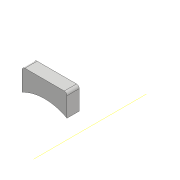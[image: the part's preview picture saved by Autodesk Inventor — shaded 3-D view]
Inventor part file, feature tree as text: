
AUTODESK INVENTOR PART (.ipt)
format: ipt  version: 2018 (Build 220112000, 112)  size: 1,485,824 bytes
history: native  units: mm
features: sketch x39, projected_geometry x37, extrude x34, fillet x13, hole x4, chamfer x4, mirror x1, other x1, revolve x1, shell x1, pattern_circular x1
ambient origin geometry x8: Origin, YZ Plane, XZ Plane, XY Plane, X Axis, Y Axis, Z Axis, Center Point
bodies: Solid1 (feature_tree), Solid2 (feature_tree)
feature tree (136):
  extrude  "Extrusion1"  Depth=45.0mm
  extrude  "Extrusion2"  Depth=2.25mm
  hole  "Hole1"  [1 undecoded]
  hole  "Hole2"  [1 undecoded]
  fillet  "Fillet1"  Radius=14.0mm
  extrude  "Extrusion3"  Depth=18.5mm
  extrude  "Extrusion4"  Depth=10.0mm
  extrude  "Extrusion5"  Depth=2.195mm
  extrude  "Extrusion6"  Depth=20.5mm
  hole  "Hole3"  [1 undecoded]
  extrude  "Extrusion7"  Depth=0.5mm
  extrude  "Extrusion8"  Depth=5.0mm TaperAngle=0.0deg
  extrude  "Extrusion9"  Depth=10.0mm
  extrude  "Extrusion10"  Depth=10.0mm
  extrude  "Extrusion11"  Depth=14.5mm
  extrude  "Extrusion12"  Depth=14.5mm
  extrude  "Extrusion13"  Depth=5.0mm
  extrude  "Extrusion14"  Depth=2.25mm
  extrude  "Extrusion15"  Depth=5.0mm
  extrude  "Extrusion16"  Depth=9.0mm
  extrude  "Extrusion17"  Depth=4.0mm
  chamfer  "Chamfer1"  Distance=1.0mm
  fillet  "Fillet7"  Radius=20.7mm
  fillet  "Fillet8"  Radius=32.0mm
  mirror  "Mirror1"
  extrude  "Extrusion18"  Depth=1.0mm TaperAngle=0.0deg
  extrude  "Extrusion19"  Depth=8.0mm
  extrude  "Extrusion20"  Depth=0.2mm TaperAngle=0.0deg
  extrude  "Extrusion21"  Depth=0.5mm TaperAngle=0.0deg
  extrude  "Extrusion22"  Depth=3.0mm TaperAngle=0.0deg
  extrude  "Extrusion23"  Depth=0.2mm TaperAngle=0.0deg
  extrude  "Extrusion24"  Depth=2.5mm TaperAngle=45.0deg
  sketch  "Sketch35"  dims[d91=8.0mm d92=0.0mm d93=3.0mm d94=0.0mm]
  other  "Work Axis1"
  revolve  "Revolution1"  [1 undecoded]
  extrude  "Extrusion25"  Depth=4.0mm TaperAngle=0.0deg
  extrude  "Extrusion26"  Depth=19.2mm TaperAngle=0.0deg
  shell  "Shell1"  Thickness=52.1mm
  extrude  "Extrusion27"  Depth=6.8mm
  extrude  "Extrusion28"  Depth=25.0mm
  chamfer  "Chamfer4"  Distance=6.9mm
  chamfer  "Chamfer5"  Distance=2.5mm
  extrude  "Extrusion29"  Depth=10.0mm
  pattern_circular  "Circular Pattern1"  Angle=90.0deg  [1 undecoded]
  fillet  "Fillet11"  Radius=5.0mm
  fillet  "Fillet12"  Radius=105.0mm
  fillet  "Fillet13"  Radius=105.0mm
  fillet  "Fillet14"  Radius=5.0mm
  chamfer  "Chamfer6"  Distance=12.8mm
  hole  "Hole6"  [1 undecoded]
  extrude  "Extrusion30"  Depth=10.0mm
  fillet  "Fillet15"  Radius=12.8mm
  extrude  "Extrusion31"  Depth=10.0mm
  fillet  "Fillet16"  Radius=20.0mm
  extrude  "Extrusion32"  Depth=10.0mm
  fillet  "Fillet17"  Radius=6.0mm
  fillet  "Fillet18"  Radius=40.0mm
  fillet  "Fillet19"  Radius=8.0mm
  fillet  "Fillet20"  Radius=40.0mm
  extrude  "Extrusion33"  Depth=10.0mm TaperAngle=0.0deg
  extrude  "Extrusion34"  Depth=10.0mm TaperAngle=45.0deg
  sketch  "Sketch1"  dims[d0=24.5mm d1=45.0mm]
  sketch  "Sketch2"  dims[d2=1.95mm d3=0.0mm d4=2.25mm]
  projected_geometry  "Projected Loop1"
  sketch  "Sketch3"  dims[d5=20.0mm d6=2.25mm]
  projected_geometry  "Projected Loop2"
  sketch  "Sketch4"  dims[d7=5.25mm d8=5.25mm d9=14.0mm]
  projected_geometry  "Projected Loop3"
  sketch  "Sketch5"  dims[d10=5.25mm d11=18.5mm]
  projected_geometry  "Projected Loop4"
  sketch  "Sketch6"  dims[d12=10.0mm d13=0.0mm d14=20.5mm]
  projected_geometry  "Projected Loop5"
  sketch  "Sketch7"  dims[d15=2.0mm d16=2.195mm]
  projected_geometry  "Projected Loop6"
  sketch  "Sketch8"  dims[d17=2.0mm]
  projected_geometry  "Projected Loop7"
  sketch  "Sketch9"  dims[d18=2.4mm d19=6.0mm d20=4.4mm d21=2.0mm d22=90.0deg d23=8.0mm d24=20.594885mm d25=20.5mm]
  projected_geometry  "Projected Loop8"
  projected_geometry  "Projected Loop9"
  sketch  "Sketch10"  dims[d26=26.65mm d27=2.0mm]
  projected_geometry  "Projected Loop10"
  projected_geometry  "Projected Loop11"
  sketch  "Sketch11"  dims[d28=2.0mm]
  projected_geometry  "Projected Loop12"
  sketch  "Sketch12"  dims[d29=2.4mm d30=6.0mm d31=4.4mm d32=2.0mm d33=90.0deg d34=8.0mm d35=20.594885mm d36=0.5mm]
  sketch  "Sketch13"  dims[d37=18.0mm d38=5.0mm d39=0.0mm]
  sketch  "Sketch14"  dims[d41=10.0mm d42=0.0mm d43=24.5mm]
  projected_geometry  "Projected Loop13"
  sketch  "Sketch15"  dims[d44=1.15mm d45=0.0mm d46=10.0mm]
  sketch  "Sketch16"  dims[d47=21.0mm d48=14.5mm]
  projected_geometry  "Projected Loop14"
  sketch  "Sketch17"  dims[d49=20.0mm d50=14.5mm]
  projected_geometry  "Projected Loop15"
  sketch  "Sketch18"  dims[d51=24.5mm d52=5.0mm]
  projected_geometry  "Projected Loop16"
  sketch  "Sketch19"  dims[d53=5.0mm d54=2.25mm]
  projected_geometry  "Projected Loop17"
  sketch  "Sketch20"  dims[d55=2.25mm d56=5.0mm]
  projected_geometry  "Projected Loop18"
  sketch  "Sketch22"  dims[d57=5.0mm d58=9.0mm]
  sketch  "Sketch25"  dims[d59=14.75mm d60=4.0mm d61=1.0mm d62=0.0mm d63=20.7mm]
  sketch  "Sketch27"  dims[d64=2.4mm d65=6.0mm d66=4.4mm d67=2.0mm d68=90.0deg d69=8.0mm d70=20.594885mm d72=32.0mm]
  projected_geometry  "Projected Loop22"
  sketch  "Sketch28"  dims[d73=5.0mm d74=0.0mm d75=1.0mm d76=0.0mm]
  projected_geometry  "Projected Loop23"
  sketch  "Sketch29"  dims[d77=12.25mm d78=0.0mm d80=8.0mm]
  projected_geometry  "Projected Loop24"
  sketch  "Sketch30"  dims[d81=4.5mm d82=0.0mm d84=0.2mm d85=0.0mm]
  projected_geometry  "Projected Loop25"
  sketch  "Sketch33"  dims[d86=21.0mm d87=0.5mm d88=0.0mm]
  projected_geometry  "Projected Loop26"
  sketch  "Sketch36"  dims[d95=5.0mm d96=0.0mm d98=0.2mm d99=0.0mm]
  projected_geometry  "Projected Loop27"
  sketch  "Sketch37"  dims[d100=0.2mm d101=0.0mm d102=2.5mm d103=2.0mm d104=45.0deg]
  projected_geometry  "Projected Loop28"
  sketch  "Sketch38"  dims[d105=1.5mm d114=0.5mm]
  projected_geometry  "Projected Loop29"
  projected_geometry  "Projected Loop30"
  projected_geometry  "Projected Loop31"
  projected_geometry  "Projected Loop32"
  sketch  "Sketch39"  dims[d115=22.55mm d116=0.0mm d128=4.0mm d129=0.0mm]
  projected_geometry  "Projected Loop33"
  projected_geometry  "Projected Loop34"
  sketch  "Sketch40"  dims[d130=4.0mm d131=0.0mm d132=19.2mm d133=0.0mm d134=52.1mm]
  projected_geometry  "Projected Loop35"
  sketch  "Sketch41"  dims[d135=6.8mm d136=0.0mm d137=9.0mm]
  projected_geometry  "Projected Loop36"
  sketch  "Sketch42"  dims[d138=9.0mm d139=25.0mm d140=6.9mm d141=0.0mm]
  sketch  "Sketch43"  dims[d142=5.2mm]
  projected_geometry  "Projected Loop37"
  sketch  "Sketch44"  dims[d143=5.2mm]
  projected_geometry  "Projected Loop38"
  sketch  "Sketch45"  dims[d144=5.2mm]
  projected_geometry  "Projected Loop39"
  sketch  "Sketch46"  dims[d145=5.2mm d146=2.5mm d147=0.0mm d148=5.0mm d149=90.0deg d150=5.0mm d151=105.0mm d152=105.0mm d153=5.0mm d154=0.0mm d156=12.8mm d157=12.8mm d158=12.8mm d159=12.8mm d160=20.0mm d161=20.0mm d162=20.0mm d163=6.0mm d164=40.0mm d165=0.0mm d166=8.0mm d167=40.0mm d168=0.0mm d169=40.0mm d170=0.0mm d178=5.1mm d179=2.45mm d180=45.0deg d181=4.1mm d182=2.45mm d183=45.0deg d184=10.0mm d185=10.0mm d186=40.0mm d187=0.0mm d188=40.0mm d189=360.0deg d191=5.1mm d192=25.0mm d193=50.0mm d194=50.0mm d195=5.0mm d196=2.0mm d197=45.0deg d198=110.0mm d199=77.781746mm d200=77.781746mm d201=6.4mm d202=6.0mm d203=12.6mm d204=2.0mm d205=90.0deg d206=8.0mm d207=20.594885mm d208=11.0mm d209=11.0mm d210=11.0mm d211=11.0mm d212=45.0mm d213=0.0mm d214=1.0mm d215=2.0mm d216=0.0mm d217=1.5mm d218=8.0mm d219=12.0mm d220=12.0mm d221=0.0mm d222=2.0mm d223=5.0mm d224=2.0mm d225=0.3mm d226=10.0mm d227=0.0mm d228=0.0mm d229=0.0mm]
  projected_geometry  "Project Cut Edges1"
note: 6 required parameter values undecoded (feature->parameter linkage not recoverable at this tier; creation-order binding heuristic only, values carry confidence <= 0.55)